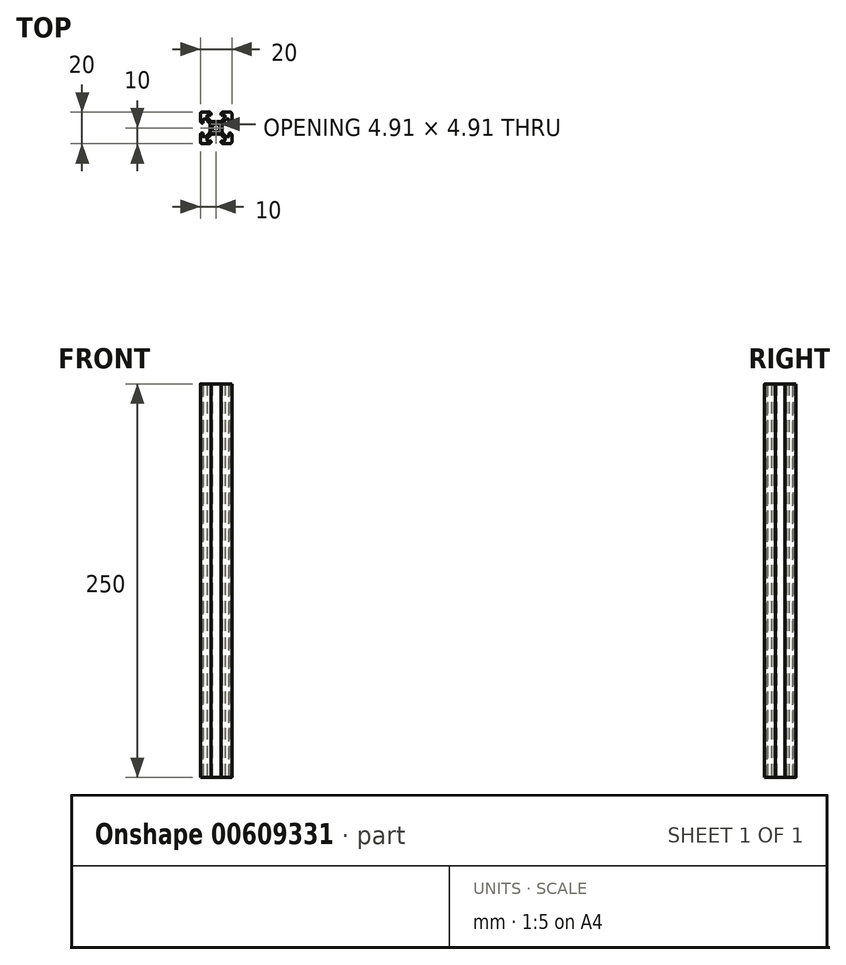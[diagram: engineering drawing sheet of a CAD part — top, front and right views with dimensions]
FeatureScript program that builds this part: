
annotation { "Feature Type Name" : "Feature", "Feature Type Description" : "" }
export const myFeature = defineFeature(function(context is Context, id is Id, definition is map)
    precondition{}
    {
        {
            var Q0;
            Q0=qCreatedBy(makeId("Top.planeOp"),FACE);
            var sketch = newSketch(context, id + "F0", { "sketchPlane" : qUnion([Q0])});
            skCircle(sketch, "E0", {"center": v(-11.7, 17.7) * mm, "radius": 2.5 * mm});
            skLineSegment(sketch, "E1", {"start": v(-14.8, 26.4) * mm, "end": v(-14.8, 26.7) * mm});
            skArc(sketch, "E2", {"start": v(-15.3, 25.9) * mm, "mid": v(-14.95, 26.05) * mm, "end": v(-14.8, 26.4) * mm});
            skLineSegment(sketch, "E3", {"start": v(-16.83, 25.9) * mm, "end": v(-15.3, 25.9) * mm});
            skArc(sketch, "E4", {"start": v(-17.33, 25.4) * mm, "mid": v(-17.18, 25.75) * mm, "end": v(-16.83, 25.9) * mm});
            skLineSegment(sketch, "E5", {"start": v(-17.33, 24.53) * mm, "end": v(-17.33, 25.4) * mm});
            skArc(sketch, "E6", {"start": v(-17.18, 24.17) * mm, "mid": v(-17.3, 24.34) * mm, "end": v(-17.33, 24.53) * mm});
            skLineSegment(sketch, "E7", {"start": v(-15.2, 22.19) * mm, "end": v(-17.18, 24.17) * mm});
            skArc(sketch, "E8", {"start": v(-13.78, 21.6) * mm, "mid": v(-14.55, 21.75) * mm, "end": v(-15.2, 22.19) * mm});
            skLineSegment(sketch, "E9", {"start": v(-9.62, 21.6) * mm, "end": v(-13.78, 21.6) * mm});
            skArc(sketch, "E10", {"start": v(-8.2, 22.19) * mm, "mid": v(-8.85, 21.75) * mm, "end": v(-9.62, 21.6) * mm});
            skLineSegment(sketch, "E11", {"start": v(-6.22, 24.17) * mm, "end": v(-8.2, 22.19) * mm});
            skArc(sketch, "E12", {"start": v(-6.07, 24.53) * mm, "mid": v(-6.1, 24.34) * mm, "end": v(-6.22, 24.17) * mm});
            skLineSegment(sketch, "E13", {"start": v(-6.07, 25.4) * mm, "end": v(-6.07, 24.53) * mm});
            skArc(sketch, "E14", {"start": v(-6.57, 25.9) * mm, "mid": v(-6.22, 25.75) * mm, "end": v(-6.07, 25.4) * mm});
            skLineSegment(sketch, "E15", {"start": v(-8.1, 25.9) * mm, "end": v(-6.57, 25.9) * mm});
            skArc(sketch, "E16", {"start": v(-8.6, 26.4) * mm, "mid": v(-8.45, 26.05) * mm, "end": v(-8.1, 25.9) * mm});
            skLineSegment(sketch, "E17", {"start": v(-8.6, 26.7) * mm, "end": v(-8.6, 26.4) * mm});
            skArc(sketch, "E18", {"start": v(-8.3, 27.16) * mm, "mid": v(-8.52, 26.97) * mm, "end": v(-8.6, 26.7) * mm});
            skArc(sketch, "E19", {"start": v(-8.06, 27.4) * mm, "mid": v(-8.16, 27.26) * mm, "end": v(-8.3, 27.16) * mm});
            skArc(sketch, "E20", {"start": v(-7.6, 27.7) * mm, "mid": v(-7.87, 27.62) * mm, "end": v(-8.06, 27.4) * mm});
            skLineSegment(sketch, "E21", {"start": v(-2.7, 27.7) * mm, "end": v(-7.6, 27.7) * mm});
            skArc(sketch, "E22", {"start": v(-1.7, 26.7) * mm, "mid": v(-2, 27.4) * mm, "end": v(-2.7, 27.7) * mm});
            skLineSegment(sketch, "E23", {"start": v(-1.7, 21.8) * mm, "end": v(-1.7, 26.7) * mm});
            skArc(sketch, "E24", {"start": v(-2, 21.34) * mm, "mid": v(-1.78, 21.53) * mm, "end": v(-1.7, 21.8) * mm});
            skArc(sketch, "E25", {"start": v(-2.24, 21.1) * mm, "mid": v(-2.14, 21.24) * mm, "end": v(-2, 21.34) * mm});
            skArc(sketch, "E26", {"start": v(-2.7, 20.8) * mm, "mid": v(-2.43, 20.88) * mm, "end": v(-2.24, 21.1) * mm});
            skLineSegment(sketch, "E27", {"start": v(-3, 20.8) * mm, "end": v(-2.7, 20.8) * mm});
            skArc(sketch, "E28", {"start": v(-3.5, 21.3) * mm, "mid": v(-3.35, 20.95) * mm, "end": v(-3, 20.8) * mm});
            skLineSegment(sketch, "E29", {"start": v(-3.5, 22.83) * mm, "end": v(-3.5, 21.3) * mm});
            skArc(sketch, "E30", {"start": v(-4, 23.33) * mm, "mid": v(-3.65, 23.18) * mm, "end": v(-3.5, 22.83) * mm});
            skLineSegment(sketch, "E31", {"start": v(-4.87, 23.33) * mm, "end": v(-4, 23.33) * mm});
            skArc(sketch, "E32", {"start": v(-5.23, 23.18) * mm, "mid": v(-5.06, 23.3) * mm, "end": v(-4.87, 23.33) * mm});
            skLineSegment(sketch, "E33", {"start": v(-7.21, 21.2) * mm, "end": v(-5.23, 23.18) * mm});
            skArc(sketch, "E34", {"start": v(-7.8, 19.78) * mm, "mid": v(-7.65, 20.55) * mm, "end": v(-7.21, 21.2) * mm});
            skLineSegment(sketch, "E35", {"start": v(-7.8, 15.62) * mm, "end": v(-7.8, 19.78) * mm});
            skArc(sketch, "E36", {"start": v(-7.21, 14.2) * mm, "mid": v(-7.65, 14.85) * mm, "end": v(-7.8, 15.62) * mm});
            skLineSegment(sketch, "E37", {"start": v(-5.23, 12.22) * mm, "end": v(-7.21, 14.2) * mm});
            skArc(sketch, "E38", {"start": v(-4.87, 12.07) * mm, "mid": v(-5.06, 12.1) * mm, "end": v(-5.23, 12.22) * mm});
            skLineSegment(sketch, "E39", {"start": v(-4, 12.07) * mm, "end": v(-4.87, 12.07) * mm});
            skArc(sketch, "E40", {"start": v(-3.5, 12.57) * mm, "mid": v(-3.65, 12.22) * mm, "end": v(-4, 12.07) * mm});
            skLineSegment(sketch, "E41", {"start": v(-3.5, 14.1) * mm, "end": v(-3.5, 12.57) * mm});
            skArc(sketch, "E42", {"start": v(-3, 14.6) * mm, "mid": v(-3.35, 14.45) * mm, "end": v(-3.5, 14.1) * mm});
            skLineSegment(sketch, "E43", {"start": v(-2.7, 14.6) * mm, "end": v(-3, 14.6) * mm});
            skArc(sketch, "E44", {"start": v(-2.24, 14.3) * mm, "mid": v(-2.43, 14.52) * mm, "end": v(-2.7, 14.6) * mm});
            skArc(sketch, "E45", {"start": v(-2, 14.06) * mm, "mid": v(-2.14, 14.16) * mm, "end": v(-2.24, 14.3) * mm});
            skArc(sketch, "E46", {"start": v(-1.7, 13.6) * mm, "mid": v(-1.78, 13.87) * mm, "end": v(-2, 14.06) * mm});
            skLineSegment(sketch, "E47", {"start": v(-1.7, 8.7) * mm, "end": v(-1.7, 13.6) * mm});
            skArc(sketch, "E48", {"start": v(-2.7, 7.7) * mm, "mid": v(-2, 8) * mm, "end": v(-1.7, 8.7) * mm});
            skLineSegment(sketch, "E49", {"start": v(-7.6, 7.7) * mm, "end": v(-2.7, 7.7) * mm});
            skArc(sketch, "E50", {"start": v(-8.06, 8) * mm, "mid": v(-7.87, 7.78) * mm, "end": v(-7.6, 7.7) * mm});
            skArc(sketch, "E51", {"start": v(-8.3, 8.24) * mm, "mid": v(-8.16, 8.14) * mm, "end": v(-8.06, 8) * mm});
            skArc(sketch, "E52", {"start": v(-8.6, 8.7) * mm, "mid": v(-8.52, 8.43) * mm, "end": v(-8.3, 8.24) * mm});
            skLineSegment(sketch, "E53", {"start": v(-8.6, 9) * mm, "end": v(-8.6, 8.7) * mm});
            skArc(sketch, "E54", {"start": v(-8.1, 9.5) * mm, "mid": v(-8.45, 9.35) * mm, "end": v(-8.6, 9) * mm});
            skLineSegment(sketch, "E55", {"start": v(-6.57, 9.5) * mm, "end": v(-8.1, 9.5) * mm});
            skArc(sketch, "E56", {"start": v(-6.07, 10) * mm, "mid": v(-6.22, 9.65) * mm, "end": v(-6.57, 9.5) * mm});
            skLineSegment(sketch, "E57", {"start": v(-6.07, 10.87) * mm, "end": v(-6.07, 10) * mm});
            skArc(sketch, "E58", {"start": v(-6.22, 11.23) * mm, "mid": v(-6.1, 11.06) * mm, "end": v(-6.07, 10.87) * mm});
            skLineSegment(sketch, "E59", {"start": v(-8.2, 13.21) * mm, "end": v(-6.22, 11.23) * mm});
            skArc(sketch, "E60", {"start": v(-9.62, 13.8) * mm, "mid": v(-8.85, 13.65) * mm, "end": v(-8.2, 13.21) * mm});
            skLineSegment(sketch, "E61", {"start": v(-13.78, 13.8) * mm, "end": v(-9.62, 13.8) * mm});
            skArc(sketch, "E62", {"start": v(-15.2, 13.21) * mm, "mid": v(-14.55, 13.65) * mm, "end": v(-13.78, 13.8) * mm});
            skLineSegment(sketch, "E63", {"start": v(-17.18, 11.23) * mm, "end": v(-15.2, 13.21) * mm});
            skArc(sketch, "E64", {"start": v(-17.33, 10.87) * mm, "mid": v(-17.3, 11.06) * mm, "end": v(-17.18, 11.23) * mm});
            skLineSegment(sketch, "E65", {"start": v(-17.33, 10) * mm, "end": v(-17.33, 10.87) * mm});
            skArc(sketch, "E66", {"start": v(-16.83, 9.5) * mm, "mid": v(-17.18, 9.65) * mm, "end": v(-17.33, 10) * mm});
            skLineSegment(sketch, "E67", {"start": v(-15.3, 9.5) * mm, "end": v(-16.83, 9.5) * mm});
            skArc(sketch, "E68", {"start": v(-14.8, 9) * mm, "mid": v(-14.95, 9.35) * mm, "end": v(-15.3, 9.5) * mm});
            skLineSegment(sketch, "E69", {"start": v(-14.8, 8.7) * mm, "end": v(-14.8, 9) * mm});
            skArc(sketch, "E70", {"start": v(-15.1, 8.24) * mm, "mid": v(-14.88, 8.43) * mm, "end": v(-14.8, 8.7) * mm});
            skArc(sketch, "E71", {"start": v(-15.34, 8) * mm, "mid": v(-15.24, 8.14) * mm, "end": v(-15.1, 8.24) * mm});
            skArc(sketch, "E72", {"start": v(-15.8, 7.7) * mm, "mid": v(-15.53, 7.78) * mm, "end": v(-15.34, 8) * mm});
            skLineSegment(sketch, "E73", {"start": v(-20.7, 7.7) * mm, "end": v(-15.8, 7.7) * mm});
            skArc(sketch, "E74", {"start": v(-21.7, 8.7) * mm, "mid": v(-21.4, 8) * mm, "end": v(-20.7, 7.7) * mm});
            skLineSegment(sketch, "E75", {"start": v(-21.7, 13.6) * mm, "end": v(-21.7, 8.7) * mm});
            skArc(sketch, "E76", {"start": v(-21.4, 14.06) * mm, "mid": v(-21.62, 13.87) * mm, "end": v(-21.7, 13.6) * mm});
            skArc(sketch, "E77", {"start": v(-21.16, 14.3) * mm, "mid": v(-21.26, 14.16) * mm, "end": v(-21.4, 14.06) * mm});
            skArc(sketch, "E78", {"start": v(-20.7, 14.6) * mm, "mid": v(-20.97, 14.52) * mm, "end": v(-21.16, 14.3) * mm});
            skLineSegment(sketch, "E79", {"start": v(-20.4, 14.6) * mm, "end": v(-20.7, 14.6) * mm});
            skArc(sketch, "E80", {"start": v(-19.9, 14.1) * mm, "mid": v(-20.05, 14.45) * mm, "end": v(-20.4, 14.6) * mm});
            skLineSegment(sketch, "E81", {"start": v(-19.9, 12.57) * mm, "end": v(-19.9, 14.1) * mm});
            skArc(sketch, "E82", {"start": v(-19.4, 12.07) * mm, "mid": v(-19.75, 12.22) * mm, "end": v(-19.9, 12.57) * mm});
            skLineSegment(sketch, "E83", {"start": v(-18.53, 12.07) * mm, "end": v(-19.4, 12.07) * mm});
            skArc(sketch, "E84", {"start": v(-18.17, 12.22) * mm, "mid": v(-18.34, 12.1) * mm, "end": v(-18.53, 12.07) * mm});
            skLineSegment(sketch, "E85", {"start": v(-16.19, 14.2) * mm, "end": v(-18.17, 12.22) * mm});
            skArc(sketch, "E86", {"start": v(-15.6, 15.62) * mm, "mid": v(-15.75, 14.85) * mm, "end": v(-16.19, 14.2) * mm});
            skLineSegment(sketch, "E87", {"start": v(-15.6, 19.78) * mm, "end": v(-15.6, 15.62) * mm});
            skArc(sketch, "E88", {"start": v(-16.19, 21.2) * mm, "mid": v(-15.75, 20.55) * mm, "end": v(-15.6, 19.78) * mm});
            skLineSegment(sketch, "E89", {"start": v(-18.17, 23.18) * mm, "end": v(-16.19, 21.2) * mm});
            skArc(sketch, "E90", {"start": v(-18.53, 23.33) * mm, "mid": v(-18.34, 23.3) * mm, "end": v(-18.17, 23.18) * mm});
            skLineSegment(sketch, "E91", {"start": v(-19.4, 23.33) * mm, "end": v(-18.53, 23.33) * mm});
            skArc(sketch, "E92", {"start": v(-19.9, 22.83) * mm, "mid": v(-19.75, 23.18) * mm, "end": v(-19.4, 23.33) * mm});
            skLineSegment(sketch, "E93", {"start": v(-19.9, 21.3) * mm, "end": v(-19.9, 22.83) * mm});
            skArc(sketch, "E94", {"start": v(-20.4, 20.8) * mm, "mid": v(-20.05, 20.95) * mm, "end": v(-19.9, 21.3) * mm});
            skLineSegment(sketch, "E95", {"start": v(-20.7, 20.8) * mm, "end": v(-20.4, 20.8) * mm});
            skArc(sketch, "E96", {"start": v(-21.16, 21.1) * mm, "mid": v(-20.97, 20.88) * mm, "end": v(-20.7, 20.8) * mm});
            skArc(sketch, "E97", {"start": v(-21.4, 21.34) * mm, "mid": v(-21.26, 21.24) * mm, "end": v(-21.16, 21.1) * mm});
            skArc(sketch, "E98", {"start": v(-21.7, 21.8) * mm, "mid": v(-21.62, 21.53) * mm, "end": v(-21.4, 21.34) * mm});
            skLineSegment(sketch, "E99", {"start": v(-21.7, 26.7) * mm, "end": v(-21.7, 21.8) * mm});
            skArc(sketch, "E100", {"start": v(-20.7, 27.7) * mm, "mid": v(-21.4, 27.4) * mm, "end": v(-21.7, 26.7) * mm});
            skLineSegment(sketch, "E101", {"start": v(-15.8, 27.7) * mm, "end": v(-20.7, 27.7) * mm});
            skArc(sketch, "E102", {"start": v(-15.34, 27.4) * mm, "mid": v(-15.53, 27.62) * mm, "end": v(-15.8, 27.7) * mm});
            skArc(sketch, "E103", {"start": v(-15.1, 27.16) * mm, "mid": v(-15.24, 27.26) * mm, "end": v(-15.34, 27.4) * mm});
            skArc(sketch, "E104", {"start": v(-14.8, 26.7) * mm, "mid": v(-14.88, 26.97) * mm, "end": v(-15.1, 27.16) * mm});
            skSolve(sketch);
        }
        {
            var Q0;
            Q0 = qSketchRegion(id + "F0", true);
            extrude(context, id + "F1", {"entities" : qUnion([Q0]), "depth" : 250 * mm, "offsetDistance" : 25 * mm});
        }
    });
